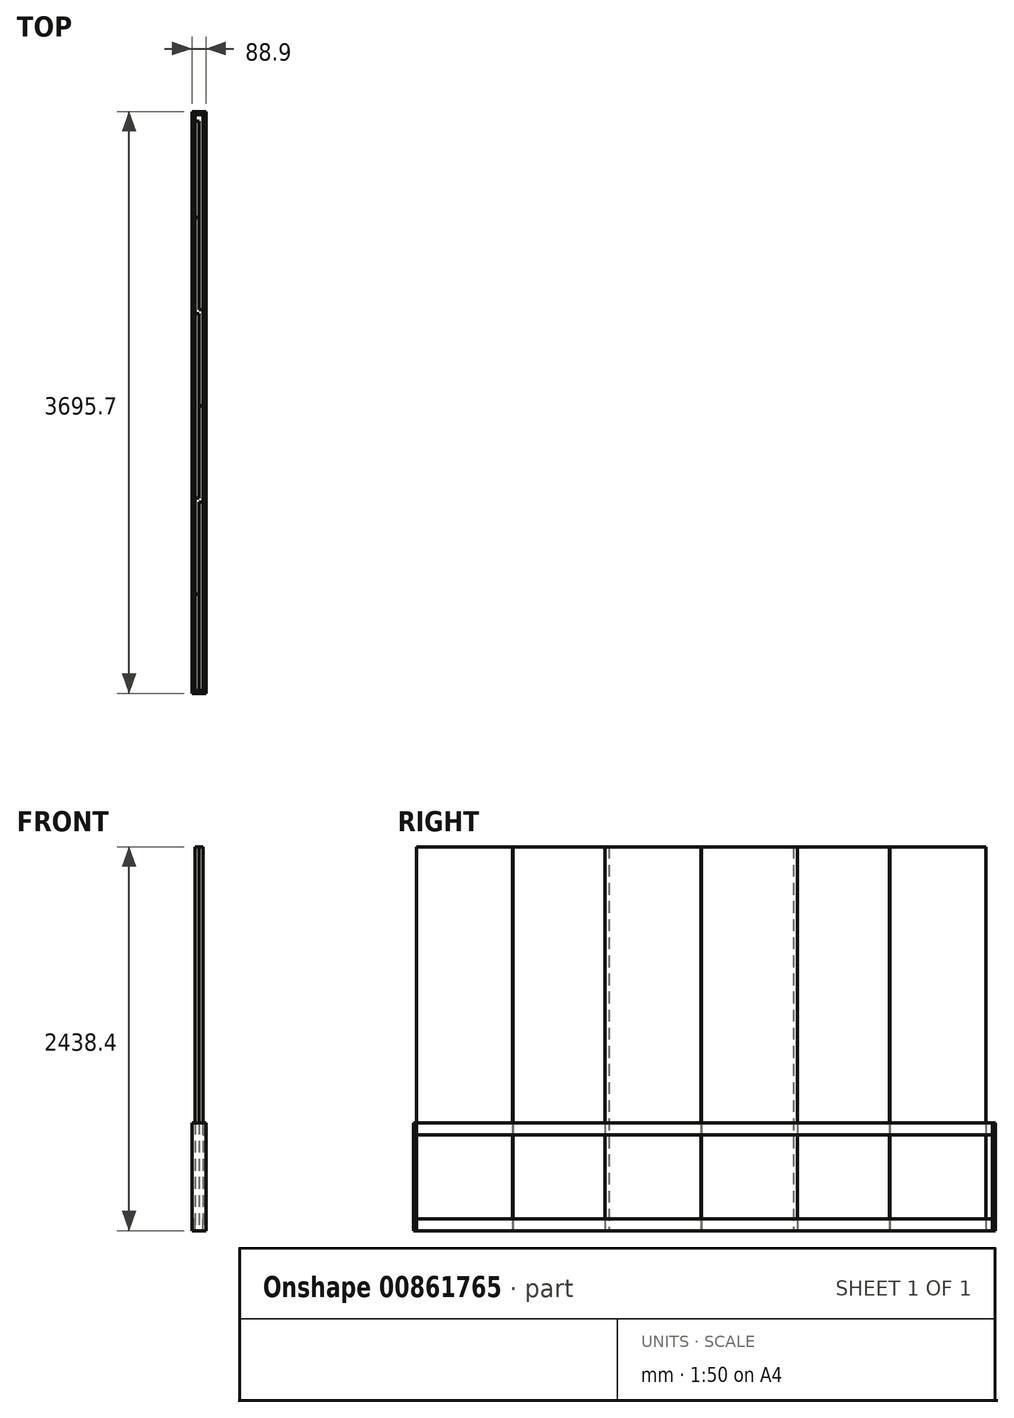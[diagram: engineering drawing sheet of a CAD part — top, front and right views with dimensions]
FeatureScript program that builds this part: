
annotation { "Feature Type Name" : "Feature", "Feature Type Description" : "" }
export const myFeature = defineFeature(function(context is Context, id is Id, definition is map)
    precondition{}
    {
        {
            var Q0;
            Q0=qCreatedBy(makeId("Front.planeOp"),FACE);
            var sketch = newSketch(context, id + "F0", { "sketchPlane" : qUnion([Q0])});
            skLineSegment(sketch, "E0.bottom", {"start": v(0, 0) * mm, "end": v(19.05, 0) * mm});
            skLineSegment(sketch, "E0.top", {"start": v(0, 76.2) * mm, "end": v(19.05, 76.2) * mm});
            skLineSegment(sketch, "E0.left", {"start": v(0, 0) * mm, "end": v(0, 76.2) * mm});
            skLineSegment(sketch, "E0.right", {"start": v(19.05, 0) * mm, "end": v(19.05, 76.2) * mm});
            skLineSegment(sketch, "E1.bottom", {"start": v(69.85, 0) * mm, "end": v(88.9, 0) * mm});
            skLineSegment(sketch, "E1.top", {"start": v(69.85, 76.2) * mm, "end": v(88.9, 76.2) * mm});
            skLineSegment(sketch, "E1.left", {"start": v(69.85, 0) * mm, "end": v(69.85, 76.2) * mm});
            skLineSegment(sketch, "E1.right", {"start": v(88.9, 0) * mm, "end": v(88.9, 76.2) * mm});
            skLineSegment(sketch, "E2.0.1.0", {"start": v(0, 685.8) * mm, "end": v(19.05, 685.8) * mm});
            skLineSegment(sketch, "E2.0.1.1", {"start": v(0, 609.6) * mm, "end": v(0, 685.8) * mm});
            skLineSegment(sketch, "E2.0.1.2", {"start": v(69.85, 609.6) * mm, "end": v(69.85, 685.8) * mm});
            skLineSegment(sketch, "E2.0.1.3", {"start": v(69.85, 685.8) * mm, "end": v(88.9, 685.8) * mm});
            skLineSegment(sketch, "E2.0.1.4", {"start": v(0, 609.6) * mm, "end": v(19.05, 609.6) * mm});
            skLineSegment(sketch, "E2.0.1.5", {"start": v(88.9, 609.6) * mm, "end": v(88.9, 685.8) * mm});
            skLineSegment(sketch, "E2.0.1.6", {"start": v(69.85, 609.6) * mm, "end": v(88.9, 609.6) * mm});
            skLineSegment(sketch, "E2.0.1.7", {"start": v(19.05, 609.6) * mm, "end": v(19.05, 685.8) * mm});
            skLineSegment(sketch, "E2.direction1", {"start": v(0, 0) * mm, "end": v(25.4, 0) * mm, "construction": true});
            skLineSegment(sketch, "E2.direction2", {"start": v(0, 0) * mm, "end": v(0, 609.6) * mm, "construction": true});
            skSolve(sketch);
        }
        {
            var Q0;
            Q0=makeQuery(id+"F0.imprint","IMPRINT",FACE,{"disambiguationData":[TD([[makeQuery(id+"F0.imprint","IMPRINT",EDGE,{"derivedFrom":sQuery(id+"F0.wireOp",EDGE,"E0.bottom")}),1.0]])]});
            var Q1;
            Q1=makeQuery(id+"F0.imprint","IMPRINT",FACE,{"disambiguationData":[TD([[makeQuery(id+"F0.imprint","IMPRINT",EDGE,{"derivedFrom":sQuery(id+"F0.wireOp",EDGE,"E1.bottom")}),1.0]])]});
            var Q2;
            Q2=makeQuery(id+"F0.imprint","IMPRINT",FACE,{"disambiguationData":[TD([[makeQuery(id+"F0.imprint","IMPRINT",EDGE,{"derivedFrom":sQuery(id+"F0.wireOp",EDGE,"E2.0.1.2")}),-1.0]])]});
            extrude(context, id + "F1", {"entities" : qUnion([Q0, Q1, Q2]), "endBound" : BoundingType.SYMMETRIC, "depth" : 3657.6 * mm, "offsetDistance" : 25.4 * mm});
        }
        {
            var Q0;
            Q0=makeQuery(id+"F1.opExtrude","SWEPT_FACE",FACE,{"disambiguationData":[OSD([sQuery(id+"F0.wireOp",EDGE,"E0.bottom")])]});
            var sketch = newSketch(context, id + "F2", { "sketchPlane" : qUnion([Q0])});
            skLineSegment(sketch, "E3.bottom", {"start": v(19.05, 1828.8) * mm, "end": v(44.45, 1828.8) * mm});
            skLineSegment(sketch, "E3.top", {"start": v(19.05, 1219.2) * mm, "end": v(44.45, 1219.2) * mm});
            skLineSegment(sketch, "E3.left", {"start": v(19.05, 1828.8) * mm, "end": v(19.05, 1219.2) * mm});
            skLineSegment(sketch, "E3.right", {"start": v(44.45, 1828.8) * mm, "end": v(44.45, 1219.2) * mm});
            skLineSegment(sketch, "E4.bottom", {"start": v(44.45, 1216.66) * mm, "end": v(19.05, 1216.66) * mm});
            skLineSegment(sketch, "E4.top", {"start": v(44.45, 607.06) * mm, "end": v(19.05, 607.06) * mm});
            skLineSegment(sketch, "E4.left", {"start": v(44.45, 1216.66) * mm, "end": v(44.45, 607.06) * mm});
            skLineSegment(sketch, "E4.right", {"start": v(19.05, 1216.66) * mm, "end": v(19.05, 607.06) * mm});
            skLineSegment(sketch, "E5.bottom", {"start": v(44.45, 632.46) * mm, "end": v(69.85, 632.46) * mm});
            skLineSegment(sketch, "E5.top", {"start": v(44.45, 22.86) * mm, "end": v(69.85, 22.86) * mm});
            skLineSegment(sketch, "E5.left", {"start": v(44.45, 632.46) * mm, "end": v(44.45, 22.86) * mm});
            skLineSegment(sketch, "E5.right", {"start": v(69.85, 632.46) * mm, "end": v(69.85, 22.86) * mm});
            skLineSegment(sketch, "E6.bottom", {"start": v(44.45, 20.32) * mm, "end": v(69.85, 20.32) * mm});
            skLineSegment(sketch, "E6.top", {"start": v(44.45, -589.28) * mm, "end": v(69.85, -589.28) * mm});
            skLineSegment(sketch, "E6.left", {"start": v(44.45, 20.32) * mm, "end": v(44.45, -589.28) * mm});
            skLineSegment(sketch, "E6.right", {"start": v(69.85, 20.32) * mm, "end": v(69.85, -589.28) * mm});
            skLineSegment(sketch, "E7.bottom", {"start": v(44.45, -563.88) * mm, "end": v(19.05, -563.88) * mm});
            skLineSegment(sketch, "E7.top", {"start": v(44.45, -1173.48) * mm, "end": v(19.05, -1173.48) * mm});
            skLineSegment(sketch, "E7.left", {"start": v(44.45, -563.88) * mm, "end": v(44.45, -1173.48) * mm});
            skLineSegment(sketch, "E7.right", {"start": v(19.05, -563.88) * mm, "end": v(19.05, -1173.48) * mm});
            skLineSegment(sketch, "E8.bottom", {"start": v(44.45, -1176.02) * mm, "end": v(19.05, -1176.02) * mm});
            skLineSegment(sketch, "E8.top", {"start": v(44.45, -1785.62) * mm, "end": v(19.05, -1785.62) * mm});
            skLineSegment(sketch, "E8.left", {"start": v(44.45, -1176.02) * mm, "end": v(44.45, -1785.62) * mm});
            skLineSegment(sketch, "E8.right", {"start": v(19.05, -1176.02) * mm, "end": v(19.05, -1785.62) * mm});
            skSolve(sketch);
        }
        {
            var Q0;
            Q0=makeQuery(id+"F2.imprint","IMPRINT",FACE,{"disambiguationData":[TD([[makeQuery(id+"F2.imprint","IMPRINT",EDGE,{"derivedFrom":sQuery(id+"F2.wireOp",EDGE,"E3.bottom")}),-1.0]])]});
            var Q1;
            Q1=makeQuery(id+"F2.imprint","IMPRINT",FACE,{"disambiguationData":[TD([[makeQuery(id+"F2.imprint","IMPRINT",EDGE,{"derivedFrom":sQuery(id+"F2.wireOp",EDGE,"E4.bottom")}),1.0]])]});
            var Q2;
            Q2=makeQuery(id+"F2.imprint","IMPRINT",FACE,{"disambiguationData":[TD([[makeQuery(id+"F2.imprint","IMPRINT",EDGE,{"derivedFrom":sQuery(id+"F2.wireOp",EDGE,"E6.bottom")}),-1.0]])]});
            var Q3;
            {var subQ3=sQuery(id+"F2.wireOp",EDGE,"E5.bottom");Q3=makeQuery(id+"F2.imprint","IMPRINT",FACE,{"disambiguationData":[TD([[makeQuery(id+"F2.imprint","IMPRINT",EDGE,{"derivedFrom":subQ3}),-1.0]])]});}
            var Q4;
            {var subQ3=sQuery(id+"F2.wireOp",EDGE,"E7.bottom");Q4=makeQuery(id+"F2.imprint","IMPRINT",FACE,{"disambiguationData":[TD([[makeQuery(id+"F2.imprint","IMPRINT",EDGE,{"derivedFrom":subQ3}),1.0]])]});}
            var Q5;
            Q5=makeQuery(id+"F2.imprint","IMPRINT",FACE,{"disambiguationData":[TD([[makeQuery(id+"F2.imprint","IMPRINT",EDGE,{"derivedFrom":sQuery(id+"F2.wireOp",EDGE,"E8.bottom")}),1.0]])]});
            extrude(context, id + "F3", {"entities" : qUnion([Q0, Q1, Q2, Q3, Q4, Q5]), "oppositeDirection" : true, "depth" : 2438.4 * mm, "offsetDistance" : 25.4 * mm});
        }
        {
            var Q0;
            Q0=makeQuery(id+"F1.opExtrude","SWEPT_FACE",FACE,{"disambiguationData":[OSD([sQuery(id+"F0.wireOp",EDGE,"E0.bottom")])]});
            var sketch = newSketch(context, id + "F4", { "sketchPlane" : qUnion([Q0])});
            skLineSegment(sketch, "E9.bottom", {"start": v(0, 1828.8) * mm, "end": v(88.9, 1828.8) * mm});
            skLineSegment(sketch, "E9.top", {"start": v(0, 1847.85) * mm, "end": v(88.9, 1847.85) * mm});
            skLineSegment(sketch, "E9.left", {"start": v(0, 1828.8) * mm, "end": v(0, 1847.85) * mm});
            skLineSegment(sketch, "E9.right", {"start": v(88.9, 1828.8) * mm, "end": v(88.9, 1847.85) * mm});
            skLineSegment(sketch, "E10.bottom", {"start": v(0, -1828.8) * mm, "end": v(88.9, -1828.8) * mm});
            skLineSegment(sketch, "E10.top", {"start": v(0, -1847.85) * mm, "end": v(88.9, -1847.85) * mm});
            skLineSegment(sketch, "E10.left", {"start": v(0, -1828.8) * mm, "end": v(0, -1847.85) * mm});
            skLineSegment(sketch, "E10.right", {"start": v(88.9, -1828.8) * mm, "end": v(88.9, -1847.85) * mm});
            skSolve(sketch);
        }
        {
            var Q0;
            Q0=makeQuery(id+"F4.imprint","IMPRINT",FACE,{"disambiguationData":[TD([[makeQuery(id+"F4.imprint","IMPRINT",EDGE,{"derivedFrom":sQuery(id+"F4.wireOp",EDGE,"E10.top")}),1.0]])]});
            var Q1;
            Q1=makeQuery(id+"F4.imprint","IMPRINT",FACE,{"disambiguationData":[TD([[makeQuery(id+"F4.imprint","IMPRINT",EDGE,{"derivedFrom":sQuery(id+"F4.wireOp",EDGE,"E9.top")}),-1.0]])]});
            var Q2;
            Q2=makeQuery(id+"F1.opExtrude","SWEPT_FACE",FACE,{"disambiguationData":[OSD([sQuery(id+"F0.wireOp",EDGE,"E2.0.1.3")])]});
            extrude(context, id + "F5", {"entities" : qUnion([Q0, Q1]), "endBound" : BoundingType.UP_TO_SURFACE, "oppositeDirection" : true, "depth" : 25.4 * mm, "endBoundEntityFace" : qUnion([Q2]), "offsetDistance" : 25.4 * mm});
        }
    });
